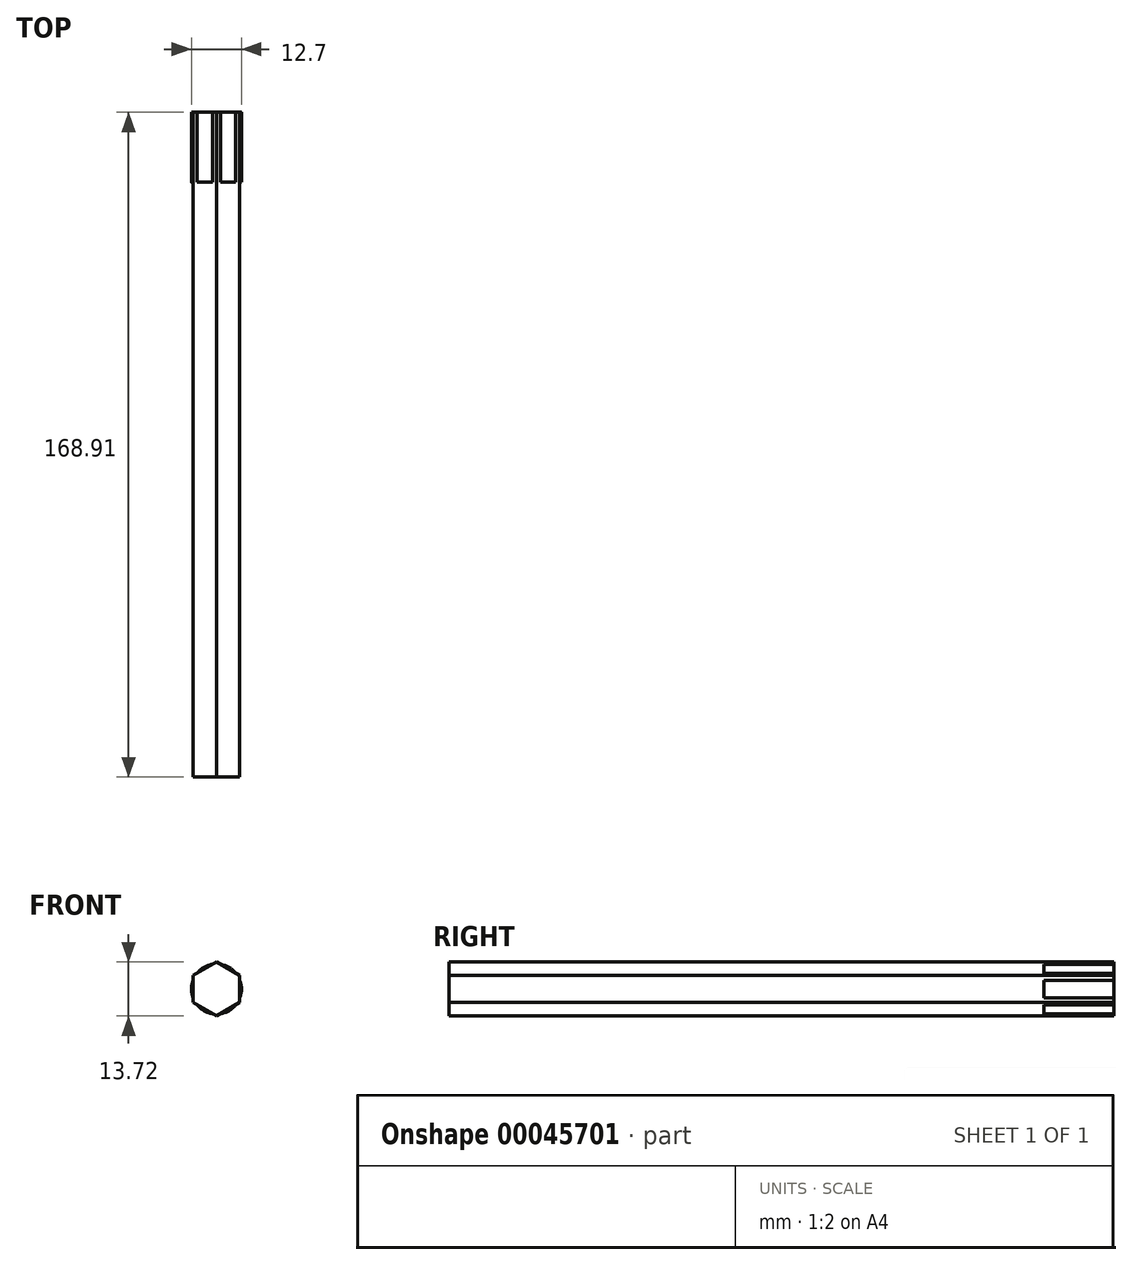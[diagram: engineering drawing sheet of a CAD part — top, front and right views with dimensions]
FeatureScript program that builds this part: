
annotation { "Feature Type Name" : "Feature", "Feature Type Description" : "" }
export const myFeature = defineFeature(function(context is Context, id is Id, definition is map)
    precondition{}
    {
        {
            var Q0;
            Q0=qCreatedBy(makeId("Front.planeOp"),FACE);
            var sketch = newSketch(context, id + "F0", { "sketchPlane" : qUnion([Q0])});
            skCircle(sketch, "E0", {"center": v(0, 0) * mm, "radius": 6.35 * mm});
            skSolve(sketch);
        }
        {
            var Q0;
            Q0=makeQuery(id+"F0.imprint","IMPRINT",FACE,{"disambiguationData":[TD([[makeQuery(id+"F0.imprint","IMPRINT",EDGE,{"derivedFrom":sQuery(id+"F0.wireOp",EDGE,"E0")}),1.0]])]});
            extrude(context, id + "F1", {"entities" : qUnion([Q0]), "depth" : 17.78 * mm});
        }
        {
            var Q0;
            Q0=qCreatedBy(makeId("Front.planeOp"),FACE);
            var sketch = newSketch(context, id + "F2", { "sketchPlane" : qUnion([Q0])});
            skCircle(sketch, "E1.cCircle", {"center": v(0, 0) * mm, "radius": 6.86 * mm, "construction": true});
            skLineSegment(sketch, "E1.0", {"start": v(0, -6.86) * mm, "end": v(-5.94, -3.43) * mm});
            skLineSegment(sketch, "E1.1", {"start": v(-5.94, -3.43) * mm, "end": v(-5.94, 3.43) * mm});
            skLineSegment(sketch, "E1.2", {"start": v(-5.94, 3.43) * mm, "end": v(0, 6.86) * mm});
            skLineSegment(sketch, "E1.3", {"start": v(0, 6.86) * mm, "end": v(5.94, 3.43) * mm});
            skLineSegment(sketch, "E1.4", {"start": v(5.94, 3.43) * mm, "end": v(5.94, -3.43) * mm});
            skLineSegment(sketch, "E1.5", {"start": v(5.94, -3.43) * mm, "end": v(0, -6.86) * mm});
            skSolve(sketch);
        }
        {
            var Q0;
            Q0=makeQuery(id+"F2.imprint","IMPRINT",FACE,{"disambiguationData":[TD([[makeQuery(id+"F2.imprint","IMPRINT",EDGE,{"derivedFrom":sQuery(id+"F2.wireOp",EDGE,"E1.0")}),-1.0]])]});
            extrude(context, id + "F3", {"entities" : qUnion([Q0]), "operationType" : NewBodyOperationType.ADD, "depth" : 168.9 * mm});
        }
    });
